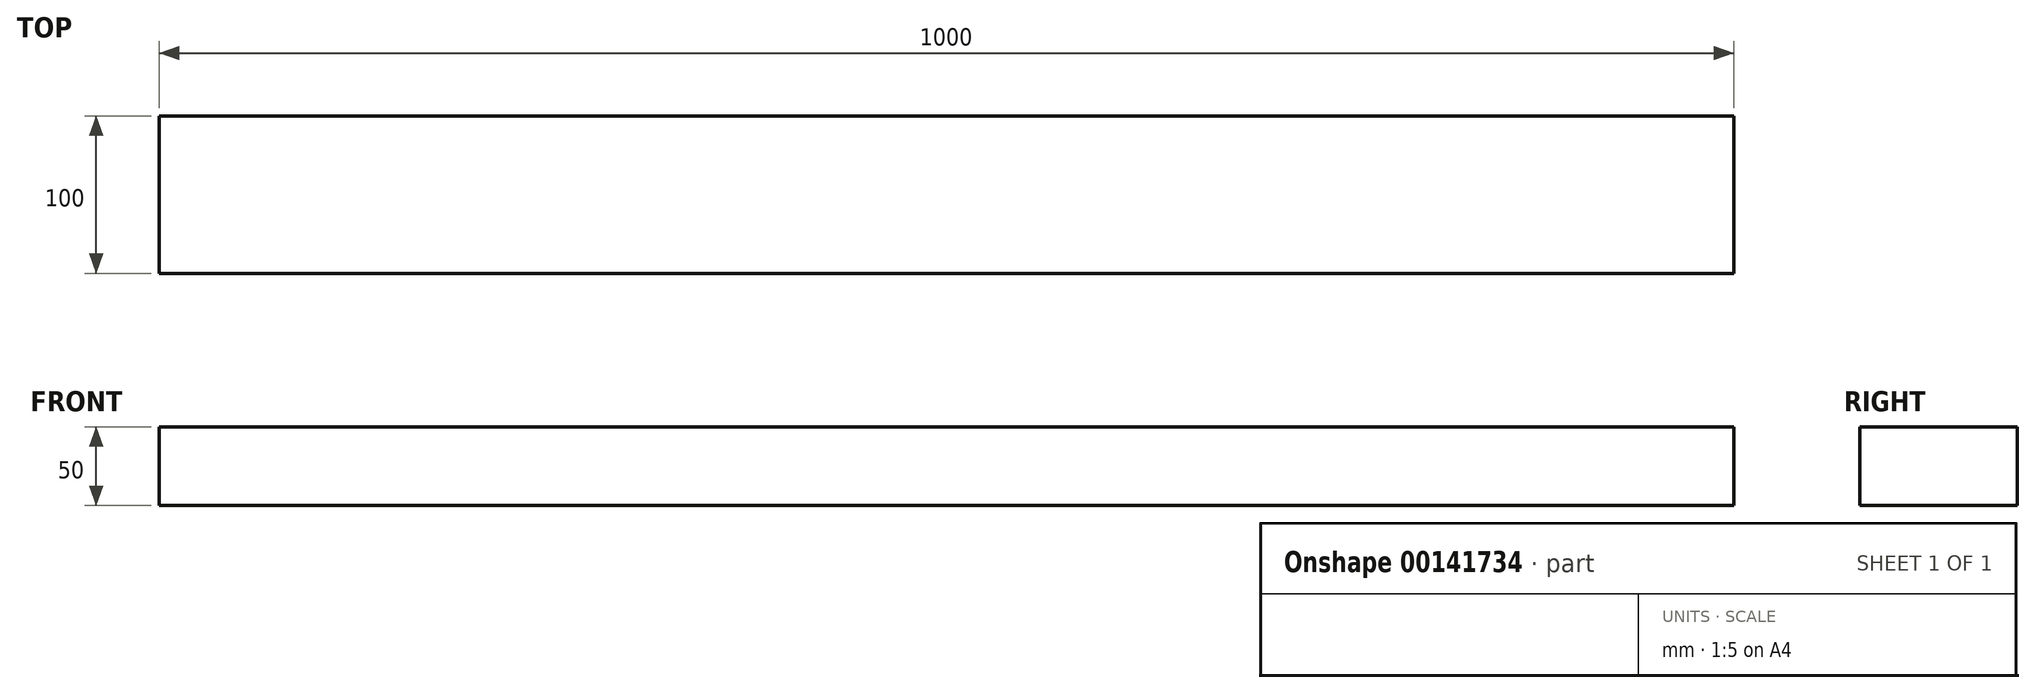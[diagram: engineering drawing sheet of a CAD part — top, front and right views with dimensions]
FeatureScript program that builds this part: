
annotation { "Feature Type Name" : "Feature", "Feature Type Description" : "" }
export const myFeature = defineFeature(function(context is Context, id is Id, definition is map)
    precondition{}
    {
        {
            var Q0;
            Q0=qCreatedBy(makeId("Right.planeOp"),FACE);
            var sketch = newSketch(context, id + "F0", { "sketchPlane" : qUnion([Q0])});
            skLineSegment(sketch, "E0.bottom", {"start": v(-50, 25) * mm, "end": v(50, 25) * mm});
            skLineSegment(sketch, "E0.top", {"start": v(-50, -25) * mm, "end": v(50, -25) * mm});
            skLineSegment(sketch, "E0.left", {"start": v(-50, 25) * mm, "end": v(-50, -25) * mm});
            skLineSegment(sketch, "E0.right", {"start": v(50, 25) * mm, "end": v(50, -25) * mm});
            skPoint(sketch, "E0.middle", {"position": v(0, 0) * mm});
            skSolve(sketch);
        }
        {
            var Q0;
            Q0=makeQuery(id+"F0.imprint","IMPRINT",FACE,{"disambiguationData":[TD([[makeQuery(id+"F0.imprint","IMPRINT",EDGE,{"derivedFrom":sQuery(id+"F0.wireOp",EDGE,"E0.bottom")}),-1.0]])]});
            extrude(context, id + "F1", {"entities" : qUnion([Q0]), "depth" : 1000 * mm});
        }
        {
            var Q0;
            Q0=makeQuery(id+"F1.opExtrude","CAP_EDGE",EDGE,{"disambiguationData":[OSD([sQuery(id+"F0.wireOp",EDGE,"E0.top")])],"isStart":false});
            chamfer(context, id + "F2", {"entities" : qUnion([Q0]), "width" : 0.1 * mm, "tangentPropagation" : true});
        }
    });
